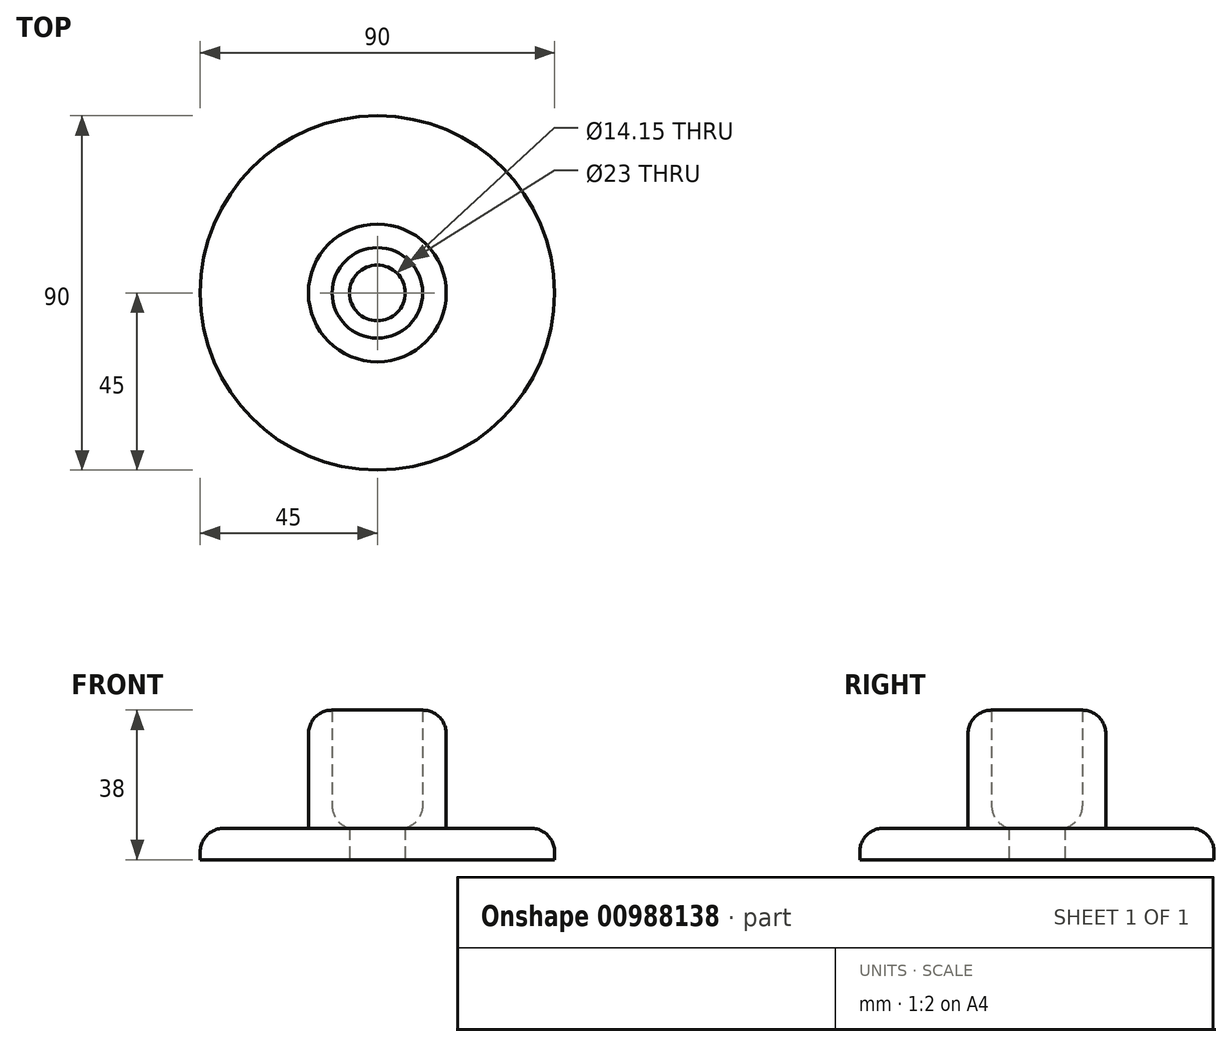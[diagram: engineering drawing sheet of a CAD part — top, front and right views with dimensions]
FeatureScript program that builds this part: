
annotation { "Feature Type Name" : "Feature", "Feature Type Description" : "" }
export const myFeature = defineFeature(function(context is Context, id is Id, definition is map)
    precondition{}
    {
        {
            var Q0;
            Q0=qCreatedBy(makeId("Top.planeOp"),FACE);
            var sketch = newSketch(context, id + "F0", { "sketchPlane" : qUnion([Q0])});
            skCircle(sketch, "E0", {"center": v(0, 0) * mm, "radius": 7.08 * mm});
            skCircle(sketch, "E1", {"center": v(0, 0) * mm, "radius": 45 * mm});
            skSolve(sketch);
        }
        {
            var Q0;
            Q0=makeQuery(id+"F0.imprint","IMPRINT",FACE,{"disambiguationData":[TD([[makeQuery(id+"F0.imprint","IMPRINT",EDGE,{"derivedFrom":sQuery(id+"F0.wireOp",EDGE,"E0")}),-1.0]])]});
            extrude(context, id + "F1", {"entities" : qUnion([Q0]), "depth" : 8 * mm, "offsetDistance" : 25 * mm});
        }
        {
            var Q0;
            Q0=makeQuery(id+"F1.opExtrude","CAP_FACE",FACE,{"disambiguationData":[OSD([sQuery(id+"F0.wireOp",EDGE,"E0"),sQuery(id+"F0.wireOp",EDGE,"E1")])],"isStart":false});
            var sketch = newSketch(context, id + "F2", { "sketchPlane" : qUnion([Q0])});
            skCircle(sketch, "E2", {"center": v(0, 0) * mm, "radius": 11.5 * mm});
            skCircle(sketch, "E3", {"center": v(0, 0) * mm, "radius": 17.5 * mm});
            skSolve(sketch);
        }
        {
            var Q0;
            Q0=makeQuery(id+"F2.imprint","IMPRINT",FACE,{"disambiguationData":[TD([[makeQuery(id+"F2.imprint","IMPRINT",EDGE,{"derivedFrom":sQuery(id+"F2.wireOp",EDGE,"E2")}),-1.0]])]});
            extrude(context, id + "F3", {"entities" : qUnion([Q0]), "operationType" : NewBodyOperationType.ADD, "depth" : 30 * mm, "offsetDistance" : 25 * mm});
        }
        {
            var Q0;
            Q0=makeQuery(id+"F3.opExtrude","CAP_EDGE",EDGE,{"disambiguationData":[OSD([sQuery(id+"F2.wireOp",EDGE,"E3")])],"isStart":true});
            var Q1;
            Q1=makeQuery(id+"F1.opExtrude","CAP_EDGE",EDGE,{"disambiguationData":[OSD([sQuery(id+"F0.wireOp",EDGE,"E1")])],"isStart":false});
            var Q2;
            Q2=makeQuery(id+"F3.opExtrude","CAP_EDGE",EDGE,{"disambiguationData":[OSD([sQuery(id+"F2.wireOp",EDGE,"E2")])],"isStart":true});
            var Q3;
            Q3=makeQuery(id+"F3.opExtrude","CAP_EDGE",EDGE,{"disambiguationData":[OSD([sQuery(id+"F2.wireOp",EDGE,"E3")])],"isStart":false});
            fillet(context, id + "F4", {"entities" : qUnion([Q0, Q1, Q2, Q3]), "radius" : 6 * mm, "tangentPropagation" : true, "allowEdgeOverflow" : false});
        }
    });
